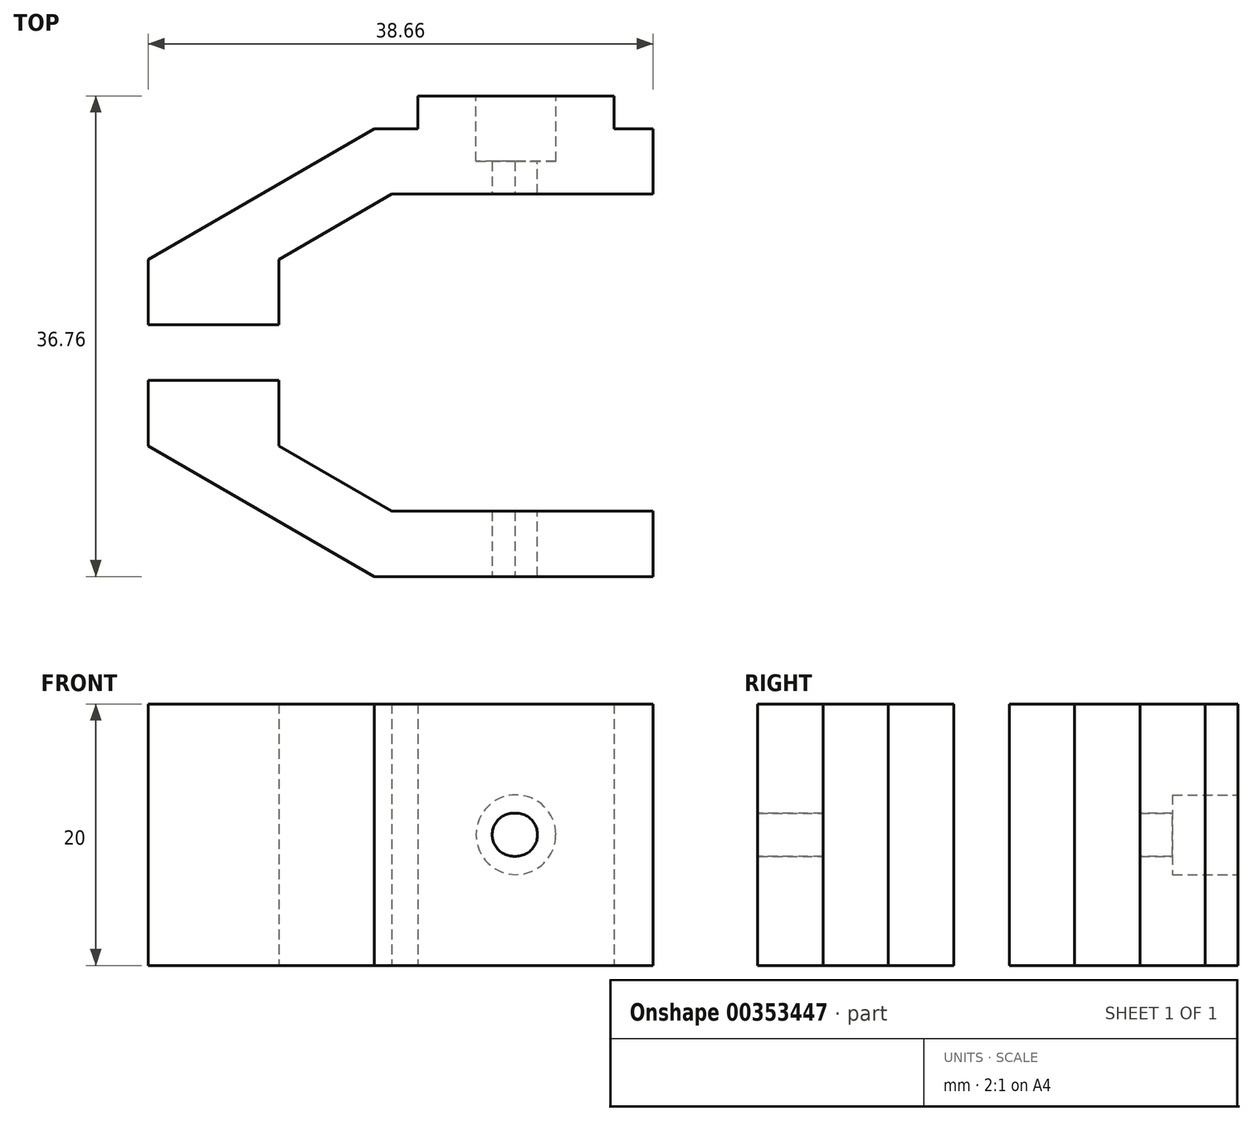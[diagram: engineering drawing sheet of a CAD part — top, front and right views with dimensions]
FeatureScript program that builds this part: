
annotation { "Feature Type Name" : "Feature", "Feature Type Description" : "" }
export const myFeature = defineFeature(function(context is Context, id is Id, definition is map)
    precondition{}
    {
        {
            var Q0;
            Q0=qCreatedBy(makeId("Top.planeOp"),FACE);
            var sketch = newSketch(context, id + "F0", { "sketchPlane" : qUnion([Q0])});
            skLineSegment(sketch, "E0.bottom", {"start": v(5, 2.5) * mm, "end": v(-5, 2.5) * mm});
            skLineSegment(sketch, "E0.top", {"start": v(5, -2.5) * mm, "end": v(-5, -2.5) * mm});
            skLineSegment(sketch, "E0.left", {"start": v(5, 2.5) * mm, "end": v(5, -2.5) * mm});
            skLineSegment(sketch, "E0.right", {"start": v(-5, 2.5) * mm, "end": v(-5, -2.5) * mm});
            skPoint(sketch, "E0.middle", {"position": v(0, 0) * mm});
            skLineSegment(sketch, "E1", {"start": v(-5, 2.5) * mm, "end": v(12.32, 12.5) * mm});
            skLineSegment(sketch, "E2", {"start": v(12.32, 12.5) * mm, "end": v(33.66, 12.5) * mm});
            skLineSegment(sketch, "E3", {"start": v(33.66, 12.5) * mm, "end": v(33.66, 7.5) * mm});
            skLineSegment(sketch, "E4", {"start": v(33.66, 7.5) * mm, "end": v(13.66, 7.5) * mm});
            skLineSegment(sketch, "E5", {"start": v(13.66, 7.5) * mm, "end": v(5, 2.5) * mm});
            skLineSegment(sketch, "E6.bottom", {"start": v(12.32, 12.5) * mm, "end": v(24.66, 12.5) * mm});
            skLineSegment(sketch, "E7.bottom", {"start": v(15.66, 12.5) * mm, "end": v(30.66, 12.5) * mm});
            skLineSegment(sketch, "E7.top", {"start": v(15.66, 15) * mm, "end": v(30.66, 15) * mm});
            skLineSegment(sketch, "E7.left", {"start": v(15.66, 12.5) * mm, "end": v(15.66, 15) * mm});
            skLineSegment(sketch, "E7.right", {"start": v(30.66, 12.5) * mm, "end": v(30.66, 15) * mm});
            skLineSegment(sketch, "E8.bottom", {"start": v(-5, -6.76) * mm, "end": v(5, -6.76) * mm});
            skLineSegment(sketch, "E8.top", {"start": v(-5, -11.76) * mm, "end": v(5, -11.76) * mm});
            skLineSegment(sketch, "E8.left", {"start": v(-5, -6.76) * mm, "end": v(-5, -11.76) * mm});
            skLineSegment(sketch, "E8.right", {"start": v(5, -6.76) * mm, "end": v(5, -11.76) * mm});
            skLineSegment(sketch, "E9", {"start": v(-5, -11.76) * mm, "end": v(12.32, -21.76) * mm});
            skLineSegment(sketch, "E10", {"start": v(12.32, -21.76) * mm, "end": v(33.66, -21.76) * mm});
            skLineSegment(sketch, "E11", {"start": v(33.66, -21.76) * mm, "end": v(33.66, -16.76) * mm});
            skLineSegment(sketch, "E12", {"start": v(33.66, -16.76) * mm, "end": v(13.66, -16.76) * mm});
            skLineSegment(sketch, "E13", {"start": v(13.66, -16.76) * mm, "end": v(5, -11.76) * mm});
            skSolve(sketch);
        }
        {
            var Q0;
            Q0 = qSketchRegion(id + "F0", true);
            extrude(context, id + "F1", {"entities" : qUnion([Q0]), "depth" : 20 * mm});
        }
        {
            var Q0;
            Q0=makeQuery(id+"F1.opExtrude","SWEPT_FACE",FACE,{"disambiguationData":[OSD([sQuery(id+"F0.wireOp",EDGE,"E7.top")])]});
            var sketch = newSketch(context, id + "F2", { "sketchPlane" : qUnion([Q0])});
            skCircle(sketch, "E14", {"center": v(-23.16, 10) * mm, "radius": 3.05 * mm});
            skPoint(sketch, "E14.centerSnap0", {"position": v(-30.66, 10) * mm});
            skPoint(sketch, "E14.centerSnap1", {"position": v(-23.16, 20) * mm});
            skSolve(sketch);
        }
        {
            var Q0;
            Q0 = qSketchRegion(id + "F2", true);
            extrude(context, id + "F3", {"entities" : qUnion([Q0]), "operationType" : NewBodyOperationType.REMOVE, "oppositeDirection" : true, "depth" : 5 * mm});
        }
        {
            var Q0;
            Q0=makeQuery(id+"F3.boolean.opBoolean","COPY",FACE,{"derivedFrom":makeQuery(id+"F3.opExtrude","CAP_FACE",FACE,{"disambiguationData":[OSD([sQuery(id+"F2.wireOp",EDGE,"E14")])],"isStart":false})});
            var sketch = newSketch(context, id + "F4", { "sketchPlane" : qUnion([Q0])});
            skCircle(sketch, "E15", {"center": v(-23.16, 10) * mm, "radius": 1.65 * mm});
            skSolve(sketch);
        }
        {
            var Q0;
            Q0 = qSketchRegion(id + "F4", true);
            extrude(context, id + "F5", {"entities" : qUnion([Q0]), "operationType" : NewBodyOperationType.REMOVE, "endBound" : BoundingType.THROUGH_ALL, "oppositeDirection" : true, "depth" : 50 * mm});
        }
        {
            var Q0;
            Q0=makeQuery(id+"F1.opExtrude","SWEPT_FACE",FACE,{"disambiguationData":[OSD([sQuery(id+"F0.wireOp",EDGE,"E10")])]});
            var sketch = newSketch(context, id + "F6", { "sketchPlane" : qUnion([Q0])});
            skCircle(sketch, "E16", {"center": v(23, 10) * mm, "radius": 1.65 * mm});
            skPoint(sketch, "E16.centerSnap0", {"position": v(12.32, 10) * mm});
            skPoint(sketch, "E16.centerSnap1", {"position": v(23, 20) * mm});
            skSolve(sketch);
        }
        {
            var Q0;
            Q0 = qSketchRegion(id + "F6", true);
            extrude(context, id + "F7", {"entities" : qUnion([Q0]), "operationType" : NewBodyOperationType.REMOVE, "endBound" : BoundingType.THROUGH_ALL, "oppositeDirection" : true, "depth" : 25 * mm});
        }
    });
